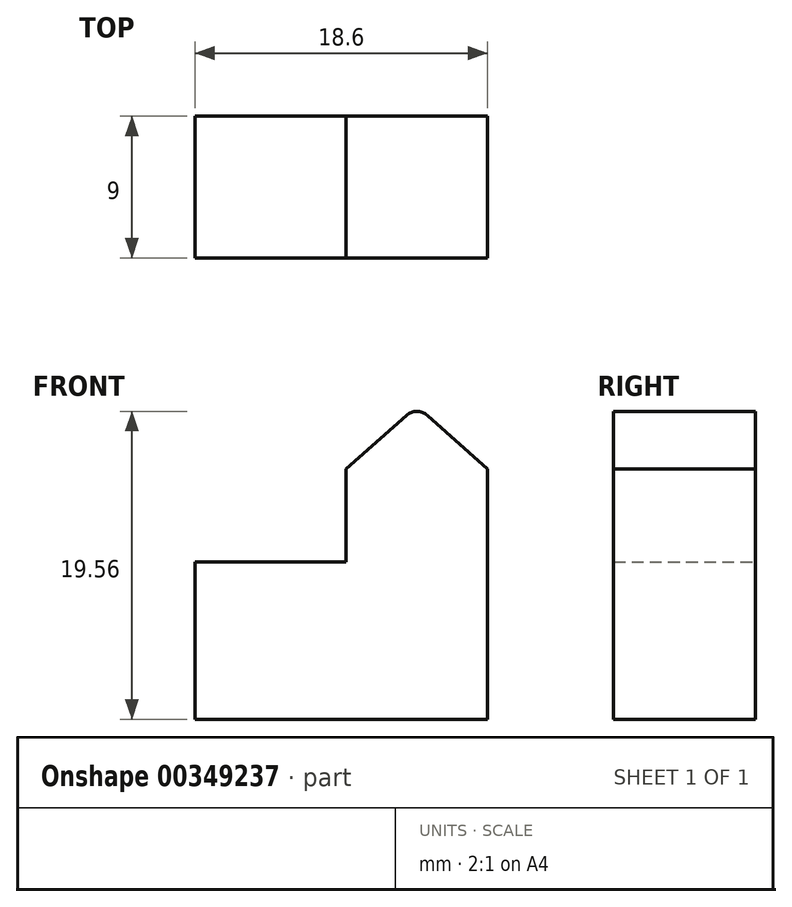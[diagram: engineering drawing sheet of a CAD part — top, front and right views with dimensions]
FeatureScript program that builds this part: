
annotation { "Feature Type Name" : "Feature", "Feature Type Description" : "" }
export const myFeature = defineFeature(function(context is Context, id is Id, definition is map)
    precondition{}
    {
        {
            var Q0;
            Q0=qCreatedBy(makeId("Top.planeOp"),FACE);
            var sketch = newSketch(context, id + "F0", { "sketchPlane" : qUnion([Q0])});
            skLineSegment(sketch, "E0.bottom", {"start": v(0, 0) * mm, "end": v(-18.6, 0) * mm});
            skLineSegment(sketch, "E0.top", {"start": v(0, -9) * mm, "end": v(-18.6, -9) * mm});
            skLineSegment(sketch, "E0.left", {"start": v(0, 0) * mm, "end": v(0, -9) * mm});
            skLineSegment(sketch, "E0.right", {"start": v(-18.6, 0) * mm, "end": v(-18.6, -9) * mm});
            skSolve(sketch);
        }
        {
            var Q0;
            Q0 = qSketchRegion(id + "F0", true);
            extrude(context, id + "F1", {"entities" : qUnion([Q0]), "depth" : 10 * mm});
        }
        {
            var Q0;
            Q0=makeQuery(id+"F1.opExtrude","CAP_FACE",FACE,{"disambiguationData":[OSD([sQuery(id+"F0.wireOp",EDGE,"E0.bottom"),sQuery(id+"F0.wireOp",EDGE,"E0.top"),sQuery(id+"F0.wireOp",EDGE,"E0.left"),sQuery(id+"F0.wireOp",EDGE,"E0.right")])],"isStart":false});
            var sketch = newSketch(context, id + "F2", { "sketchPlane" : qUnion([Q0])});
            skLineSegment(sketch, "E1.bottom", {"start": v(0, -9) * mm, "end": v(-9, -9) * mm});
            skLineSegment(sketch, "E1.top", {"start": v(0, 0) * mm, "end": v(-9, 0) * mm});
            skLineSegment(sketch, "E1.left", {"start": v(0, -9) * mm, "end": v(0, 0) * mm});
            skLineSegment(sketch, "E1.right", {"start": v(-9, -9) * mm, "end": v(-9, 0) * mm});
            skSolve(sketch);
        }
        {
            var Q0;
            Q0=makeQuery(id+"F2.imprint","IMPRINT",FACE,{"disambiguationData":[TD([[makeQuery(id+"F2.imprint","IMPRINT",EDGE,{"derivedFrom":sQuery(id+"F2.wireOp",EDGE,"E1.bottom")}),-1.0]])]});
            extrude(context, id + "F3", {"entities" : qUnion([Q0]), "operationType" : NewBodyOperationType.ADD, "depth" : 5.9 * mm});
        }
        {
            var Q0;
            Q0=makeQuery(id+"F3.boolean.opBoolean","MERGE",FACE,{"derivedFrom":[makeQuery(id+"F1.opExtrude","SWEPT_FACE",FACE,{"disambiguationData":[OSD([sQuery(id+"F0.wireOp",EDGE,"E0.top")])]}),makeQuery(id+"F3.opExtrude","SWEPT_FACE",FACE,{"disambiguationData":[OSD([sQuery(id+"F2.wireOp",EDGE,"E1.bottom")])]})]});
            var sketch = newSketch(context, id + "F4", { "sketchPlane" : qUnion([Q0])});
            skLineSegment(sketch, "E2", {"start": v(-4.5, 15.9) * mm, "end": v(-4.5, 19.9) * mm, "construction": true});
            skLineSegment(sketch, "E3", {"start": v(-9, 15.9) * mm, "end": v(-4.5, 19.9) * mm});
            skLineSegment(sketch, "E4", {"start": v(0, 15.9) * mm, "end": v(-4.5, 19.9) * mm});
            skLineSegment(sketch, "E5", {"start": v(-9, 15.9) * mm, "end": v(0, 15.9) * mm});
            skSolve(sketch);
        }
        {
            var Q0;
            Q0 = qSketchRegion(id + "F4", true);
            var Q1;
            Q1=makeQuery(id+"F3.boolean.opBoolean","MERGE",FACE,{"derivedFrom":[makeQuery(id+"F1.opExtrude","SWEPT_FACE",FACE,{"disambiguationData":[OSD([sQuery(id+"F0.wireOp",EDGE,"E0.bottom")])]}),makeQuery(id+"F3.opExtrude","SWEPT_FACE",FACE,{"disambiguationData":[OSD([sQuery(id+"F2.wireOp",EDGE,"E1.top")])]})]});
            extrude(context, id + "F5", {"entities" : qUnion([Q0]), "operationType" : NewBodyOperationType.ADD, "endBound" : BoundingType.UP_TO_SURFACE, "oppositeDirection" : true, "endBoundEntityFace" : qUnion([Q1]), "depth" : 25 * mm});
        }
        {
            var Q0;
            Q0=makeQuery(id+"F5.opExtrude","SWEPT_EDGE",EDGE,{"disambiguationData":[OSD([sQuery(id+"F4.wireOp",EDGE,"E3"),sQuery(id+"F4.wireOp",EDGE,"E4")])]});
            var Q1;
            Q1=makeQuery(id+"F3.opExtrude","CAP_EDGE",EDGE,{"disambiguationData":[OSD([sQuery(id+"F2.wireOp",EDGE,"E1.right")])],"isStart":true});
            fillet(context, id + "F6", {"entities" : qUnion([Q0, Q1]), "radius" : 1 * mm, "tangentPropagation" : true, "allowEdgeOverflow" : false});
        }
    });
